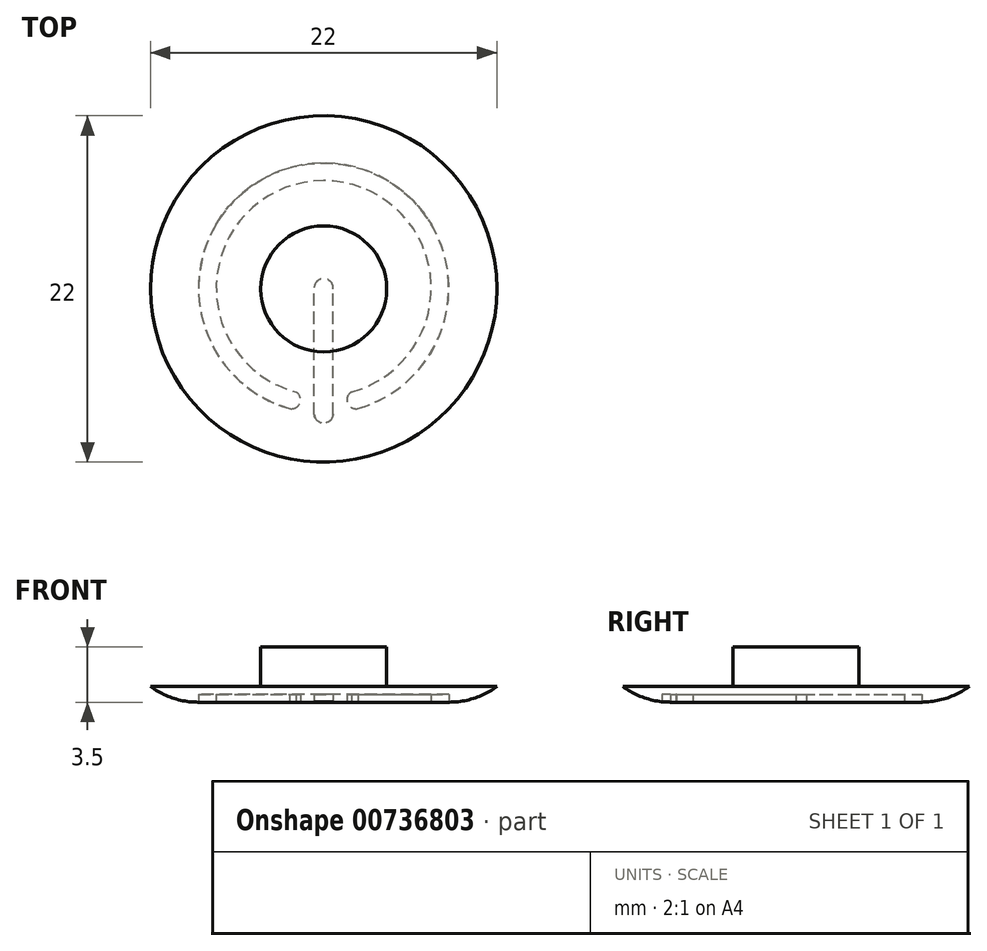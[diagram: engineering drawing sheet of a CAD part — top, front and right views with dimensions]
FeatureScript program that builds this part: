
annotation { "Feature Type Name" : "Feature", "Feature Type Description" : "" }
export const myFeature = defineFeature(function(context is Context, id is Id, definition is map)
    precondition{}
    {
        {
            var Q0;
            Q0=qCreatedBy(makeId("Top.planeOp"),FACE);
            var sketch = newSketch(context, id + "F0", { "sketchPlane" : qUnion([Q0])});
            skCircle(sketch, "E0", {"center": v(0, 0) * mm, "radius": 11 * mm});
            skCircle(sketch, "E1", {"center": v(0, 0) * mm, "radius": 4 * mm});
            skSolve(sketch);
        }
        {
            var Q0;
            Q0=makeQuery(id+"F0.imprint","IMPRINT",FACE,{"disambiguationData":[TD([[makeQuery(id+"F0.imprint","IMPRINT",EDGE,{"derivedFrom":sQuery(id+"F0.wireOp",EDGE,"E1")}),1.0]])]});
            extrude(context, id + "F1", {"entities" : qUnion([Q0]), "depth" : 3.5 * mm, "offsetDistance" : 25.4 * mm});
        }
        {
            var Q0;
            Q0=makeQuery(id+"F0.imprint","IMPRINT",FACE,{"disambiguationData":[TD([[makeQuery(id+"F0.imprint","IMPRINT",EDGE,{"derivedFrom":sQuery(id+"F0.wireOp",EDGE,"E0")}),1.0]])]});
            extrude(context, id + "F2", {"entities" : qUnion([Q0]), "operationType" : NewBodyOperationType.ADD, "depth" : 1 * mm, "offsetDistance" : 25.4 * mm});
        }
        {
            var Q0;
            Q0=makeQuery(id+"F0.imprint","IMPRINT",FACE,{"disambiguationData":[TD([[makeQuery(id+"F0.imprint","IMPRINT",EDGE,{"derivedFrom":sQuery(id+"F0.wireOp",EDGE,"E0")}),1.0]])]});
            var sketch = newSketch(context, id + "F3", { "sketchPlane" : qUnion([Q0])});
            skPoint(sketch, "E2", {"position": v(-1.76, -6.55) * mm});
            skPoint(sketch, "E3.MirrorP", {"position": v(1.76, -6.55) * mm});
            skArc(sketch, "E4", {"start": v(1.76, -6.55) * mm, "mid": v(0, 6.87) * mm, "end": v(-1.76, -6.55) * mm});
            skLineSegment(sketch, "E5", {"start": v(-0.6, -7.96) * mm, "end": v(-0.6, 0) * mm});
            skArc(sketch, "E6", {"start": v(-0.6, -7.96) * mm, "mid": v(0, -8.52) * mm, "end": v(0.6, -7.96) * mm});
            skArc(sketch, "E7", {"start": v(0.6, 0) * mm, "mid": v(0, 0.65) * mm, "end": v(-0.6, 0) * mm});
            skLineSegment(sketch, "E8.MirrorCS", {"start": v(0.6, -7.96) * mm, "end": v(0.6, 0) * mm});
            skArc(sketch, "E9", {"start": v(2.19, -7.6) * mm, "mid": v(0, 8) * mm, "end": v(-2.19, -7.6) * mm});
            skArc(sketch, "E10", {"start": v(-2.22, -7.59) * mm, "mid": v(-1.52, -7.28) * mm, "end": v(-1.76, -6.55) * mm});
            skArc(sketch, "E11.MirrorCS", {"start": v(2.22, -7.59) * mm, "mid": v(1.52, -7.28) * mm, "end": v(1.76, -6.55) * mm});
            skSolve(sketch);
        }
        {
            var Q0;
            {var subQ0=sQuery(id+"F3.wireOp",EDGE,"E6");Q0=makeQuery(id+"F3.imprint","IMPRINT",FACE,{"disambiguationData":[TD([[makeQuery(id+"F3.imprint","IMPRINT",EDGE,{"derivedFrom":subQ0}),1.0]])]});}
            var Q1;
            {var subQ0=sQuery(id+"F3.wireOp",EDGE,"E7");Q1=makeQuery(id+"F3.imprint","IMPRINT",FACE,{"disambiguationData":[TD([[makeQuery(id+"F3.imprint","IMPRINT",EDGE,{"derivedFrom":subQ0}),1.0]])]});}
            var Q2;
            {var subQ1=sQuery(id+"F3.wireOp",EDGE,"E4");Q2=makeQuery(id+"F3.imprint","IMPRINT",FACE,{"disambiguationData":[TD([[makeQuery(id+"F3.imprint","IMPRINT",EDGE,{"derivedFrom":subQ1}),-1.0]])]});}
            extrude(context, id + "F4", {"entities" : qUnion([Q0, Q1, Q2]), "operationType" : NewBodyOperationType.REMOVE, "depth" : .5 * mm, "offsetDistance" : 25.4 * mm});
        }
        {
            var Q0;
            Q0=makeQuery(id+"F2.opExtrude","CAP_EDGE",EDGE,{"disambiguationData":[OSD([sQuery(id+"F0.wireOp",EDGE,"E0")])],"isStart":true});
            fillet(context, id + "F5", {"entities" : qUnion([Q0]), "radius" : 5.08 * mm, "tangentPropagation" : true, "allowEdgeOverflow" : false});
        }
    });
